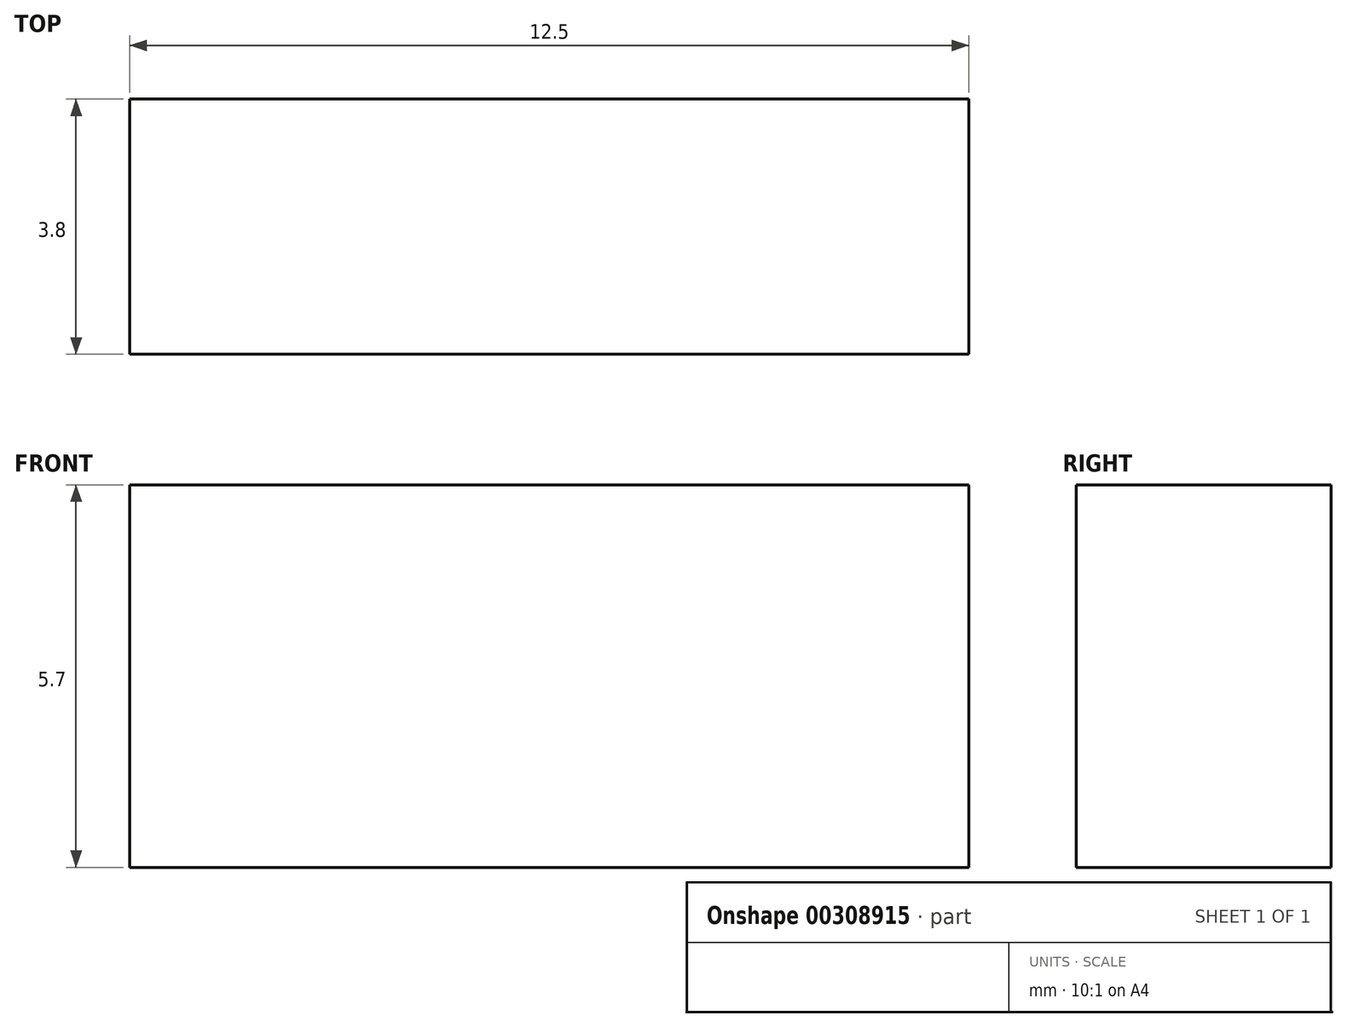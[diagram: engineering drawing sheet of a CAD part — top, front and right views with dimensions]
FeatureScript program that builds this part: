
annotation { "Feature Type Name" : "Feature", "Feature Type Description" : "" }
export const myFeature = defineFeature(function(context is Context, id is Id, definition is map)
    precondition{}
    {
        {
            var Q0;
            Q0=qCreatedBy(makeId("Front.planeOp"),FACE);
            var sketch = newSketch(context, id + "F0", { "sketchPlane" : qUnion([Q0])});
            skLineSegment(sketch, "E0.bottom", {"start": v(0, 0) * mm, "end": v(12.5, 0) * mm});
            skLineSegment(sketch, "E0.top", {"start": v(0, 5.7) * mm, "end": v(12.5, 5.7) * mm});
            skLineSegment(sketch, "E0.left", {"start": v(0, 0) * mm, "end": v(0, 5.7) * mm});
            skLineSegment(sketch, "E0.right", {"start": v(12.5, 0) * mm, "end": v(12.5, 5.7) * mm});
            skSolve(sketch);
        }
        {
            var Q0;
            Q0 = qSketchRegion(id + "F0", true);
            extrude(context, id + "F1", {"entities" : qUnion([Q0]), "depth" : 3.8 * mm});
        }
    });
